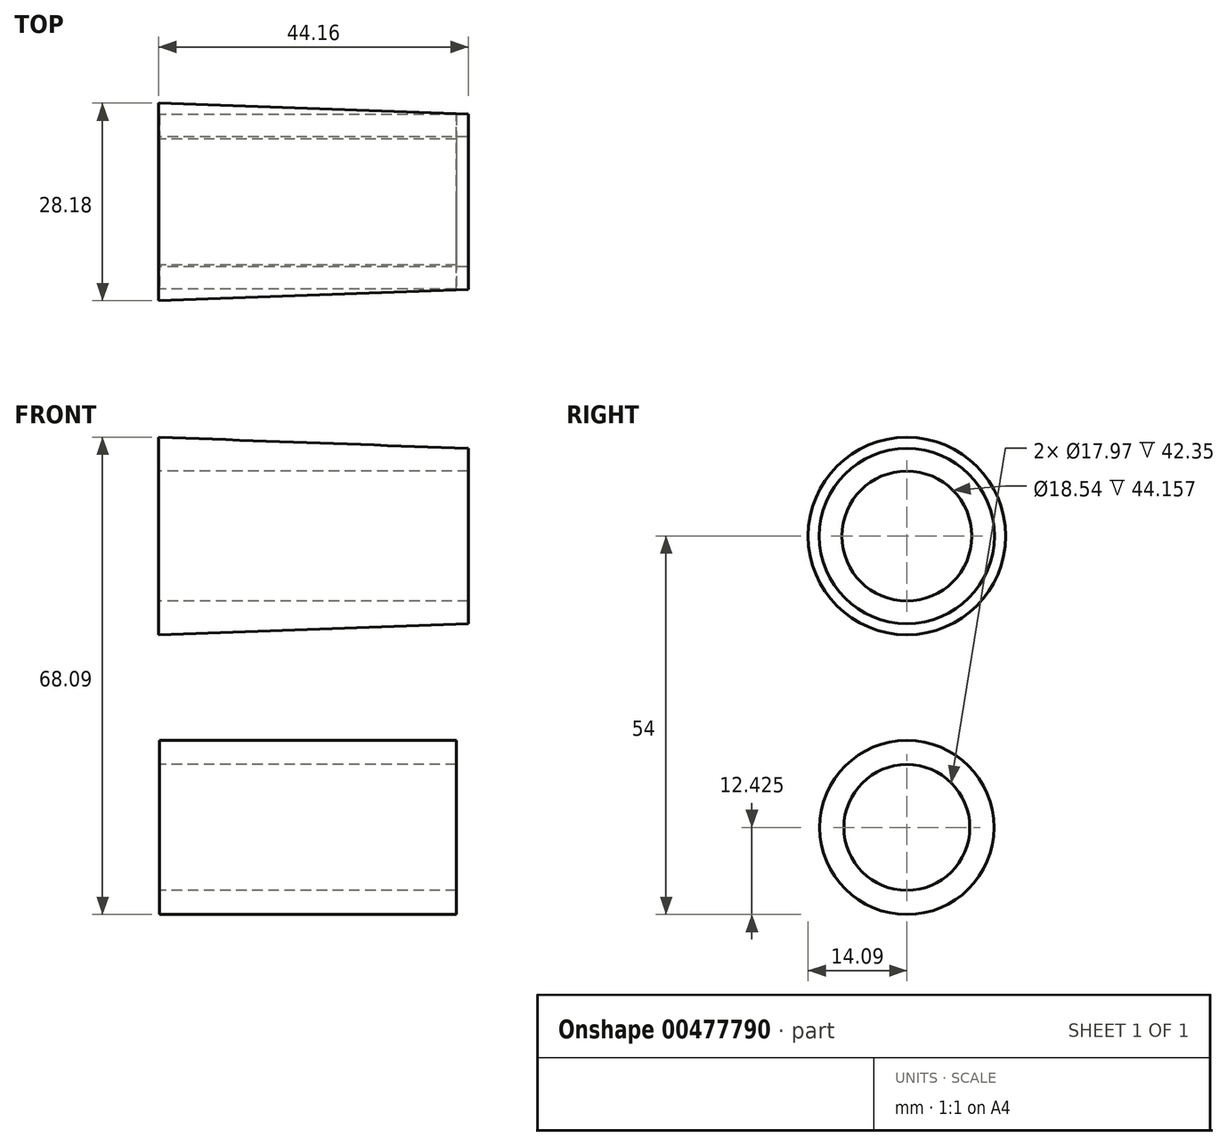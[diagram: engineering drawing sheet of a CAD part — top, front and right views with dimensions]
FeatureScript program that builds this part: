
annotation { "Feature Type Name" : "Feature", "Feature Type Description" : "" }
export const myFeature = defineFeature(function(context is Context, id is Id, definition is map)
    precondition{}
    {
        {
            var Q0;
            Q0=qCreatedBy(makeId("Front.planeOp"),FACE);
            var sketch = newSketch(context, id + "F0", { "sketchPlane" : qUnion([Q0])});
            skPoint(sketch, "E0.middle", {"position": v(0, 0) * mm});
            skLineSegment(sketch, "E1", {"start": v(-22.08, 9.27) * mm, "end": v(22.08, 9.27) * mm});
            skLineSegment(sketch, "E2", {"start": v(-27.1, 0) * mm, "end": v(29.2, 0) * mm});
            skLineSegment(sketch, "E3", {"start": v(22.08, 12.5) * mm, "end": v(22.08, 9.27) * mm});
            skLineSegment(sketch, "E4", {"start": v(22.08, 12.5) * mm, "end": v(-22.08, 14.1) * mm});
            skLineSegment(sketch, "E5", {"start": v(-22.08, 14.1) * mm, "end": v(-22.08, 9.27) * mm});
            skSolve(sketch);
        }
        {
            var Q0;
            Q0=makeQuery(id+"F0.imprint","IMPRINT",FACE,{"disambiguationData":[TD([[makeQuery(id+"F0.imprint","IMPRINT",EDGE,{"derivedFrom":sQuery(id+"F0.wireOp",EDGE,"E1")}),1.0]])]});
            var Q1;
            Q1=sQuery(id+"F0.wireOp",EDGE,"E2");
            revolve(context, id + "F1", {"entities" : qUnion([Q0]), "axis" : qUnion([Q1]), "revolveType" : RevolveType.FULL});
        }
        {
            var Q0;
            Q0=qCreatedBy(makeId("Front.planeOp"),FACE);
            var sketch = newSketch(context, id + "F2", { "sketchPlane" : qUnion([Q0])});
            skLineSegment(sketch, "E6", {"start": v(-36.82, -41.57) * mm, "end": v(49.56, -41.57) * mm, "construction": true});
            skLineSegment(sketch, "E7.bottom", {"start": v(-21.99, -29.15) * mm, "end": v(20.36, -29.15) * mm});
            skLineSegment(sketch, "E7.top", {"start": v(-21.99, -32.6) * mm, "end": v(20.36, -32.6) * mm});
            skLineSegment(sketch, "E7.left", {"start": v(-21.99, -29.15) * mm, "end": v(-21.99, -32.6) * mm});
            skLineSegment(sketch, "E7.right", {"start": v(20.36, -29.15) * mm, "end": v(20.36, -32.6) * mm});
            skSolve(sketch);
        }
        {
            var Q0;
            Q0=makeQuery(id+"F2.imprint","IMPRINT",FACE,{"disambiguationData":[TD([[makeQuery(id+"F2.imprint","IMPRINT",EDGE,{"derivedFrom":sQuery(id+"F2.wireOp",EDGE,"E7.bottom")}),-1.0]])]});
            var Q1;
            Q1=sQuery(id+"F2.wireOp",EDGE,"E6");
            revolve(context, id + "F3", {"entities" : qUnion([Q0]), "axis" : qUnion([Q1]), "revolveType" : RevolveType.FULL});
        }
        {
            var Q0;
            Q0=makeQuery(id+"F3.opRevolve","SWEPT_BODY",BODY,{"disambiguationData":[OSD([sQuery(id+"F2.wireOp",EDGE,"E7.bottom"),sQuery(id+"F2.wireOp",EDGE,"E7.top"),sQuery(id+"F2.wireOp",EDGE,"E7.left"),sQuery(id+"F2.wireOp",EDGE,"E7.right")])]});
            transform(context, id + "F4", {"entities" : qUnion([Q0]), "transformType" : TransformType.TRANSLATION_3D, "dx" : 0 * mm, "dy" : 0 * mm, "dz" : 0 * mm, "makeCopy" : true});
        }
    });
